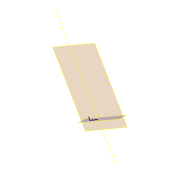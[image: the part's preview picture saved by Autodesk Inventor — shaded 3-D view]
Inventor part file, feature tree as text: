
AUTODESK INVENTOR PART (.ipt)
format: ipt  version: 2016 (Build 200138000, 138)  size: 68,096 bytes
history: native  units: in
note: dims shown in document units (in); Inventor stores cm internally (conversion verified against a paired STEP export)
features: other x6, plane x2, sketch x1
ambient origin geometry x8: Origin, YZ Plane, XZ Plane, XY Plane, X Axis, Y Axis, Z Axis, Center Point
feature tree (9):
  other  "skeleton.ipt"
  other  "Blocks"
  plane  "Work Plane1"
  other  "Work Axis1"
  other  "Work Axis2"
  other  "L3_ankle"
  sketch  "Sketch1"  dims[d0=0.3937in d1=11.811in d2=9.4488in d5=1.9291in d6=5.9055in d12=1.9291in d13=1.5748in d3=90.0deg]
  plane  "Work Plane2"
  other  "L3_ankle:1"
